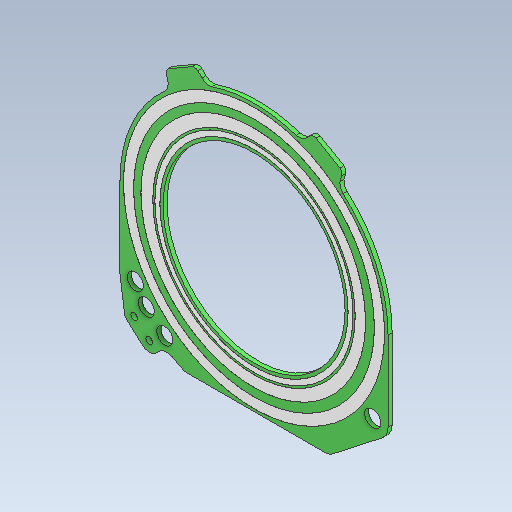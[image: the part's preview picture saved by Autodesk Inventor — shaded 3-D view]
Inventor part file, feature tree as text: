
AUTODESK INVENTOR PART (.ipt)
format: ipt  version: 2020 (Build 240168000, 168)  size: 202,752 bytes
history: native  units: in
note: dims shown in document units (in); Inventor stores cm internally (conversion verified against a paired STEP export)
features: extrude x1
ambient origin geometry x8: Origin, YZ Plane, XZ Plane, XY Plane, X Axis, Y Axis, Z Axis, Center Point
bodies: Solid1 (feature_tree)
feature tree (1):
  extrude  "Extrude2"  [1 undecoded]
note: 1 required parameter value undecoded (feature->parameter linkage not recoverable at this tier; creation-order binding heuristic only, values carry confidence <= 0.55)
